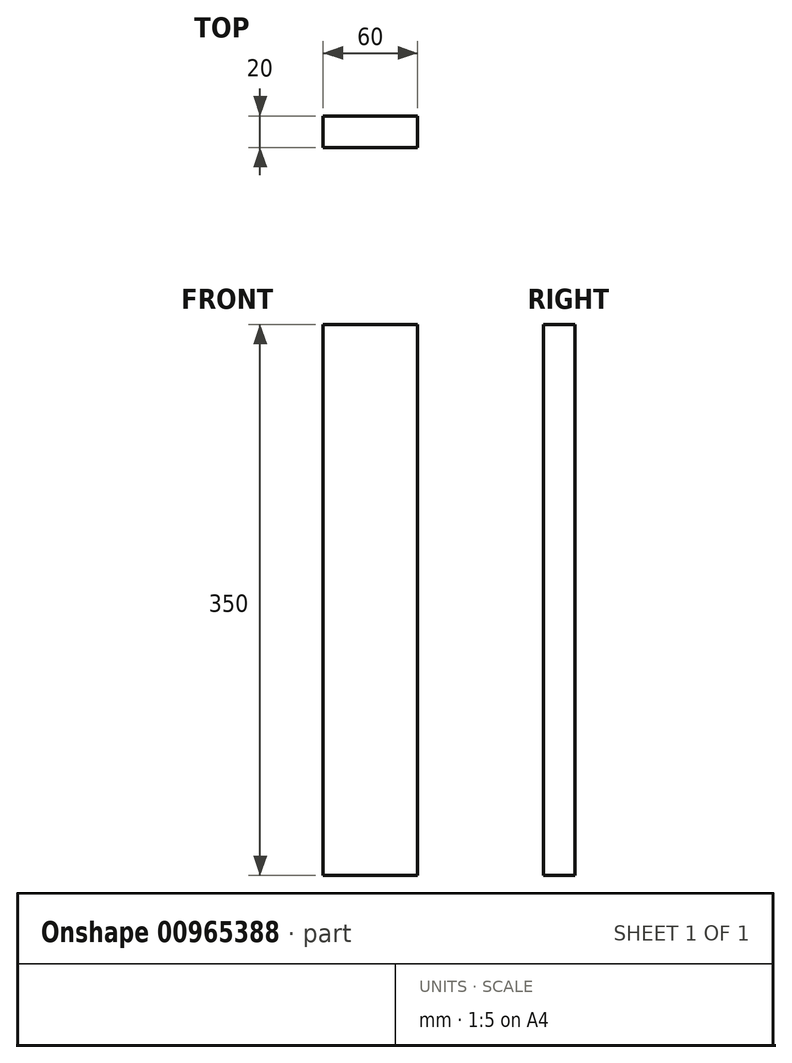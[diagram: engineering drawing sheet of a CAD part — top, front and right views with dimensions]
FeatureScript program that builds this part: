
annotation { "Feature Type Name" : "Feature", "Feature Type Description" : "" }
export const myFeature = defineFeature(function(context is Context, id is Id, definition is map)
    precondition{}
    {
        {
            var Q0;
            Q0=qCreatedBy(makeId("Top.planeOp"),FACE);
            var sketch = newSketch(context, id + "F0", { "sketchPlane" : qUnion([Q0])});
            skLineSegment(sketch, "E0.bottom", {"start": v(30, 10) * mm, "end": v(-30, 10) * mm});
            skLineSegment(sketch, "E0.top", {"start": v(30, -10) * mm, "end": v(-30, -10) * mm});
            skLineSegment(sketch, "E0.left", {"start": v(30, 10) * mm, "end": v(30, -10) * mm});
            skLineSegment(sketch, "E0.right", {"start": v(-30, 10) * mm, "end": v(-30, -10) * mm});
            skPoint(sketch, "E0.middle", {"position": v(0, 0) * mm});
            skSolve(sketch);
        }
        {
            var Q0;
            Q0=makeQuery(id+"F0.imprint","IMPRINT",FACE,{"disambiguationData":[TD([[makeQuery(id+"F0.imprint","IMPRINT",EDGE,{"derivedFrom":sQuery(id+"F0.wireOp",EDGE,"E0.bottom")}),1.0]])]});
            extrude(context, id + "F1", {"entities" : qUnion([Q0]), "depth" : 350 * mm, "offsetDistance" : 25 * mm});
        }
    });
